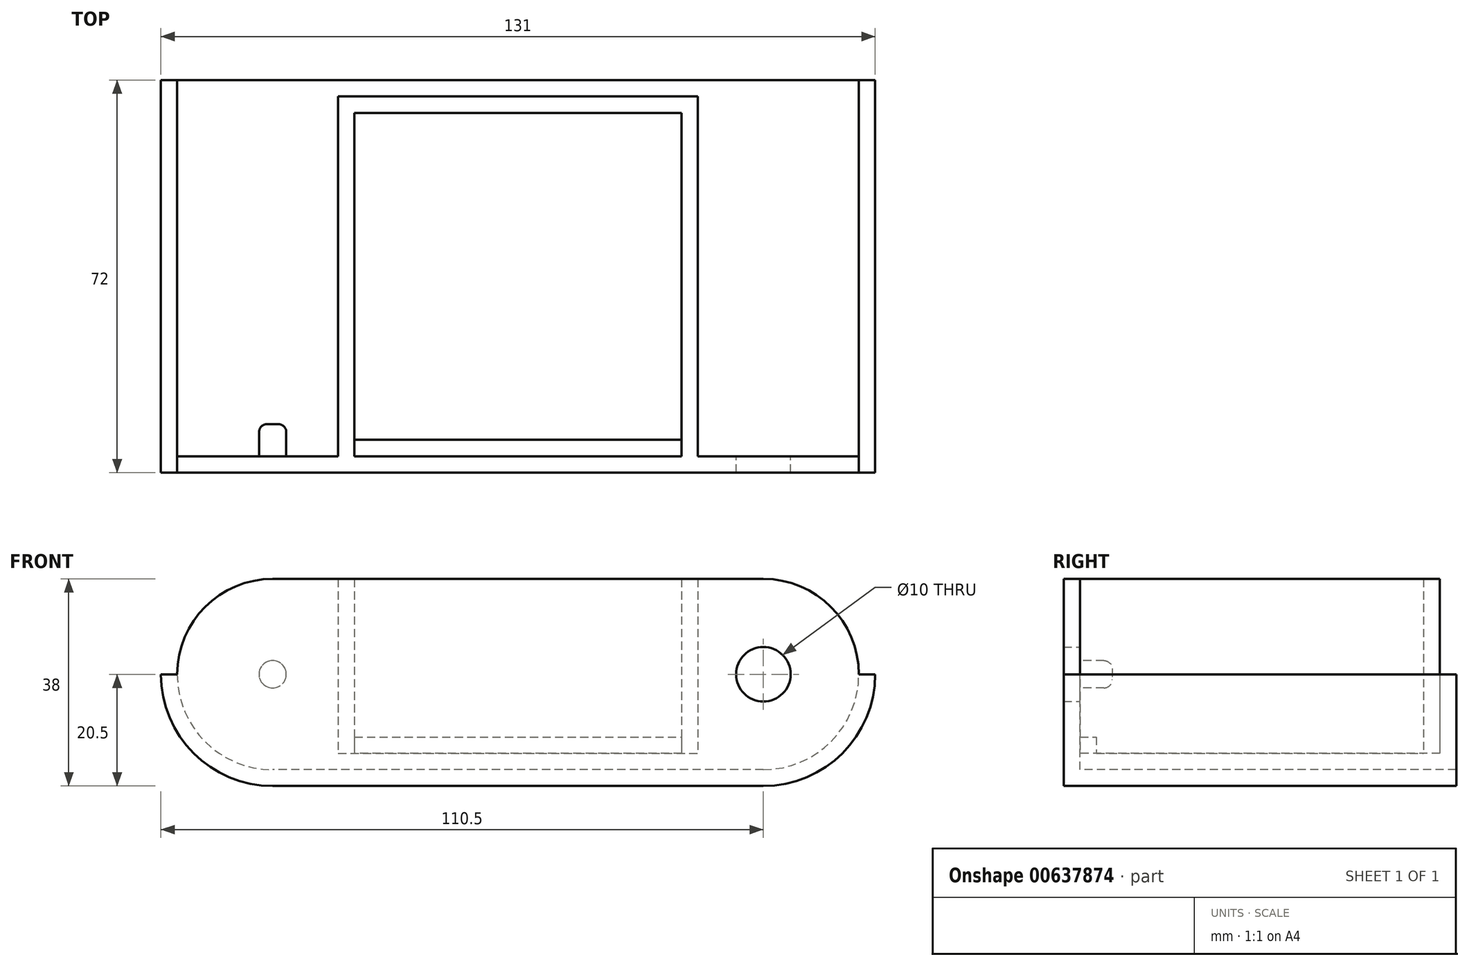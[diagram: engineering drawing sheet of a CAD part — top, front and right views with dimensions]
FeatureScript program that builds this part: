
annotation { "Feature Type Name" : "Feature", "Feature Type Description" : "" }
export const myFeature = defineFeature(function(context is Context, id is Id, definition is map)
    precondition{}
    {
        {
            var Q0;
            Q0=qCreatedBy(makeId("Front.planeOp"),FACE);
            var sketch = newSketch(context, id + "F0", { "sketchPlane" : qUnion([Q0])});
            skLineSegment(sketch, "E0.bottom", {"start": v(45, 17.5) * mm, "end": v(-45, 17.5) * mm});
            skLineSegment(sketch, "E0.top", {"start": v(45, -17.5) * mm, "end": v(-45, -17.5) * mm});
            skPoint(sketch, "E0.middle", {"position": v(0, 0) * mm});
            skArc(sketch, "E1", {"start": v(-45, 17.5) * mm, "mid": v(-62.5, 0) * mm, "end": v(-45, -17.5) * mm});
            skArc(sketch, "E2", {"start": v(45, -17.5) * mm, "mid": v(62.5, 0) * mm, "end": v(45, 17.5) * mm});
            skCircle(sketch, "E3", {"center": v(45, 0) * mm, "radius": 5 * mm});
            skSolve(sketch);
        }
        {
            var Q0;
            Q0=qSketchRegion(id+"F0",true);
            extrude(context, id + "F1", {"entities" : qUnion([Q0]), "depth" : 3 * mm, "offsetDistance" : 25 * mm});
        }
        {
            var Q0;
            Q0=makeQuery(id+"F1.opExtrude","CAP_FACE",FACE,{"disambiguationData":[OSD([sQuery(id+"F0.wireOp",EDGE,"E0.bottom"),sQuery(id+"F0.wireOp",EDGE,"E0.top"),sQuery(id+"F0.wireOp",EDGE,"E1"),sQuery(id+"F0.wireOp",EDGE,"E2"),sQuery(id+"F0.wireOp",EDGE,"E3")])],"isStart":true});
            var sketch = newSketch(context, id + "F2", { "sketchPlane" : qUnion([Q0])});
            skLineSegment(sketch, "E4.bottom", {"start": v(33, -11.5) * mm, "end": v(-33, -11.5) * mm});
            skLineSegment(sketch, "E4.top", {"start": v(33, -14.5) * mm, "end": v(-33, -14.5) * mm});
            skLineSegment(sketch, "E4.left", {"start": v(33, -11.5) * mm, "end": v(33, -14.5) * mm});
            skLineSegment(sketch, "E4.right", {"start": v(-33, -11.5) * mm, "end": v(-33, -14.5) * mm});
            skPoint(sketch, "E4.middle", {"position": v(0, -13) * mm});
            skSolve(sketch);
        }
        {
            var Q0;
            Q0=qSketchRegion(id+"F2",true);
            extrude(context, id + "F3", {"entities" : qUnion([Q0]), "operationType" : NewBodyOperationType.ADD, "depth" : 66 * mm, "offsetDistance" : 25 * mm});
        }
        {
            var Q0;
            Q0=makeQuery(id+"F3.opExtrude","SWEPT_FACE",FACE,{"disambiguationData":[OSD([sQuery(id+"F2.wireOp",EDGE,"E4.top")])]});
            var sketch = newSketch(context, id + "F4", { "sketchPlane" : qUnion([Q0])});
            skLineSegment(sketch, "E5", {"start": v(0, 0) * mm, "end": v(0, -66) * mm, "construction": true});
            skLineSegment(sketch, "E6.bottom", {"start": v(30, -3) * mm, "end": v(-30, -3) * mm});
            skLineSegment(sketch, "E6.top", {"start": v(30, -63) * mm, "end": v(-30, -63) * mm});
            skLineSegment(sketch, "E6.left", {"start": v(30, -3) * mm, "end": v(30, -63) * mm});
            skLineSegment(sketch, "E6.right", {"start": v(-30, -3) * mm, "end": v(-30, -63) * mm});
            skPoint(sketch, "E6.middle", {"position": v(0, -33) * mm});
            skSolve(sketch);
        }
        {
            var Q0;
            Q0=qSketchRegion(id+"F4",true);
            extrude(context, id + "F5", {"entities" : qUnion([Q0]), "operationType" : NewBodyOperationType.REMOVE, "oppositeDirection" : true, "depth" : 25 * mm, "offsetDistance" : 25 * mm});
        }
        {
            var Q0;
            Q0=makeQuery(id+"F1.opExtrude","CAP_FACE",FACE,{"disambiguationData":[OSD([sQuery(id+"F0.wireOp",EDGE,"E0.bottom"),sQuery(id+"F0.wireOp",EDGE,"E0.top"),sQuery(id+"F0.wireOp",EDGE,"E1"),sQuery(id+"F0.wireOp",EDGE,"E2"),sQuery(id+"F0.wireOp",EDGE,"E3")])],"isStart":true});
            var sketch = newSketch(context, id + "F6", { "sketchPlane" : qUnion([Q0])});
            skLineSegment(sketch, "E7", {"start": v(45, 17.5) * mm, "end": v(45, -17.5) * mm, "construction": true});
            skCircle(sketch, "E8", {"center": v(45, 0) * mm, "radius": 2.5 * mm});
            skSolve(sketch);
        }
        {
            var Q0;
            Q0=qSketchRegion(id+"F6",true);
            extrude(context, id + "F7", {"entities" : qUnion([Q0]), "operationType" : NewBodyOperationType.ADD, "depth" : 5.9 * mm, "offsetDistance" : 25 * mm});
        }
        {
            var Q0;
            Q0=makeQuery(id+"F7.opExtrude","CAP_EDGE",EDGE,{"disambiguationData":[OSD([sQuery(id+"F6.wireOp",EDGE,"E8")])],"isStart":false});
            fillet(context, id + "F8", {"entities" : qUnion([Q0]), "radius" : 1.5 * mm, "tangentPropagation" : true, "allowEdgeOverflow" : false});
        }
        {
            var Q0;
            Q0=makeQuery(id+"F1.opExtrude","CAP_FACE",FACE,{"disambiguationData":[OSD([sQuery(id+"F0.wireOp",EDGE,"E0.bottom"),sQuery(id+"F0.wireOp",EDGE,"E0.top"),sQuery(id+"F0.wireOp",EDGE,"E1"),sQuery(id+"F0.wireOp",EDGE,"E2"),sQuery(id+"F0.wireOp",EDGE,"E3")])],"isStart":true});
            var sketch = newSketch(context, id + "F9", { "sketchPlane" : qUnion([Q0])});
            skLineSegment(sketch, "E9", {"start": v(62.5, 0) * mm, "end": v(65.5, 0) * mm});
            skLineSegment(sketch, "E10", {"start": v(-62.5, 0) * mm, "end": v(-65.5, 0) * mm});
            skLineSegment(sketch, "E11", {"start": v(-45, -17.5) * mm, "end": v(-45, -20.5) * mm});
            skLineSegment(sketch, "E12", {"start": v(45, -17.5) * mm, "end": v(45, -20.5) * mm});
            skArc(sketch, "E13", {"start": v(-62.5, 0) * mm, "mid": v(-57.37, -12.37) * mm, "end": v(-45, -17.5) * mm});
            skArc(sketch, "E14", {"start": v(45, -17.5) * mm, "mid": v(57.37, -12.37) * mm, "end": v(62.5, 0) * mm});
            skArc(sketch, "E15", {"start": v(45, -20.5) * mm, "mid": v(59.5, -14.5) * mm, "end": v(65.5, 0) * mm});
            skArc(sketch, "E16", {"start": v(-65.5, 0) * mm, "mid": v(-59.5, -14.5) * mm, "end": v(-45, -20.5) * mm});
            skLineSegment(sketch, "E17", {"start": v(-45, -20.5) * mm, "end": v(45, -20.5) * mm});
            skLineSegment(sketch, "E18", {"start": v(45, -17.5) * mm, "end": v(-45, -17.5) * mm});
            skSolve(sketch);
        }
        {
            var Q0;
            Q0=qSketchRegion(id+"F9",true);
            extrude(context, id + "F10", {"entities" : qUnion([Q0]), "operationType" : NewBodyOperationType.ADD, "depth" : 69 * mm, "offsetDistance" : 25 * mm, "hasSecondDirection" : true, "secondDirectionOppositeDirection" : true, "secondDirectionDepth" : 3 * mm});
        }
        {
            var Q0;
            Q0=makeQuery(id+"F3.opExtrude","SWEPT_FACE",FACE,{"disambiguationData":[OSD([sQuery(id+"F2.wireOp",EDGE,"E4.bottom")])]});
            var sketch = newSketch(context, id + "F11", { "sketchPlane" : qUnion([Q0])});
            skLineSegment(sketch, "E19.bottom", {"start": v(-33, 66) * mm, "end": v(33, 66) * mm});
            skLineSegment(sketch, "E19.top", {"start": v(-33, 63) * mm, "end": v(33, 63) * mm});
            skLineSegment(sketch, "E19.left", {"start": v(-33, 66) * mm, "end": v(-33, 63) * mm});
            skLineSegment(sketch, "E19.right", {"start": v(33, 66) * mm, "end": v(33, 63) * mm});
            skSolve(sketch);
        }
        {
            var Q0;
            Q0=qSketchRegion(id+"F11",true);
            extrude(context, id + "F12", {"entities" : qUnion([Q0]), "operationType" : NewBodyOperationType.ADD, "depth" : 29 * mm, "offsetDistance" : 25 * mm});
        }
        {
            var Q0;
            Q0=makeQuery(id+"F3.opExtrude","SWEPT_FACE",FACE,{"disambiguationData":[OSD([sQuery(id+"F2.wireOp",EDGE,"E4.bottom")])]});
            var sketch = newSketch(context, id + "F13", { "sketchPlane" : qUnion([Q0])});
            skLineSegment(sketch, "E20.bottom", {"start": v(-33, 0) * mm, "end": v(-30, 0) * mm});
            skLineSegment(sketch, "E20.top", {"start": v(-33, 63) * mm, "end": v(-30, 63) * mm});
            skLineSegment(sketch, "E20.left", {"start": v(-33, 0) * mm, "end": v(-33, 63) * mm});
            skLineSegment(sketch, "E20.right", {"start": v(-30, 0) * mm, "end": v(-30, 63) * mm});
            skLineSegment(sketch, "E21.bottom", {"start": v(33, 0) * mm, "end": v(30, 0) * mm});
            skLineSegment(sketch, "E21.top", {"start": v(33, 63) * mm, "end": v(30, 63) * mm});
            skLineSegment(sketch, "E21.left", {"start": v(33, 0) * mm, "end": v(33, 63) * mm});
            skLineSegment(sketch, "E21.right", {"start": v(30, 0) * mm, "end": v(30, 63) * mm});
            skSolve(sketch);
        }
        {
            var Q0;
            Q0=qSketchRegion(id+"F13",true);
            extrude(context, id + "F14", {"entities" : qUnion([Q0]), "operationType" : NewBodyOperationType.ADD, "depth" : 29 * mm, "offsetDistance" : 25 * mm});
        }
    });
